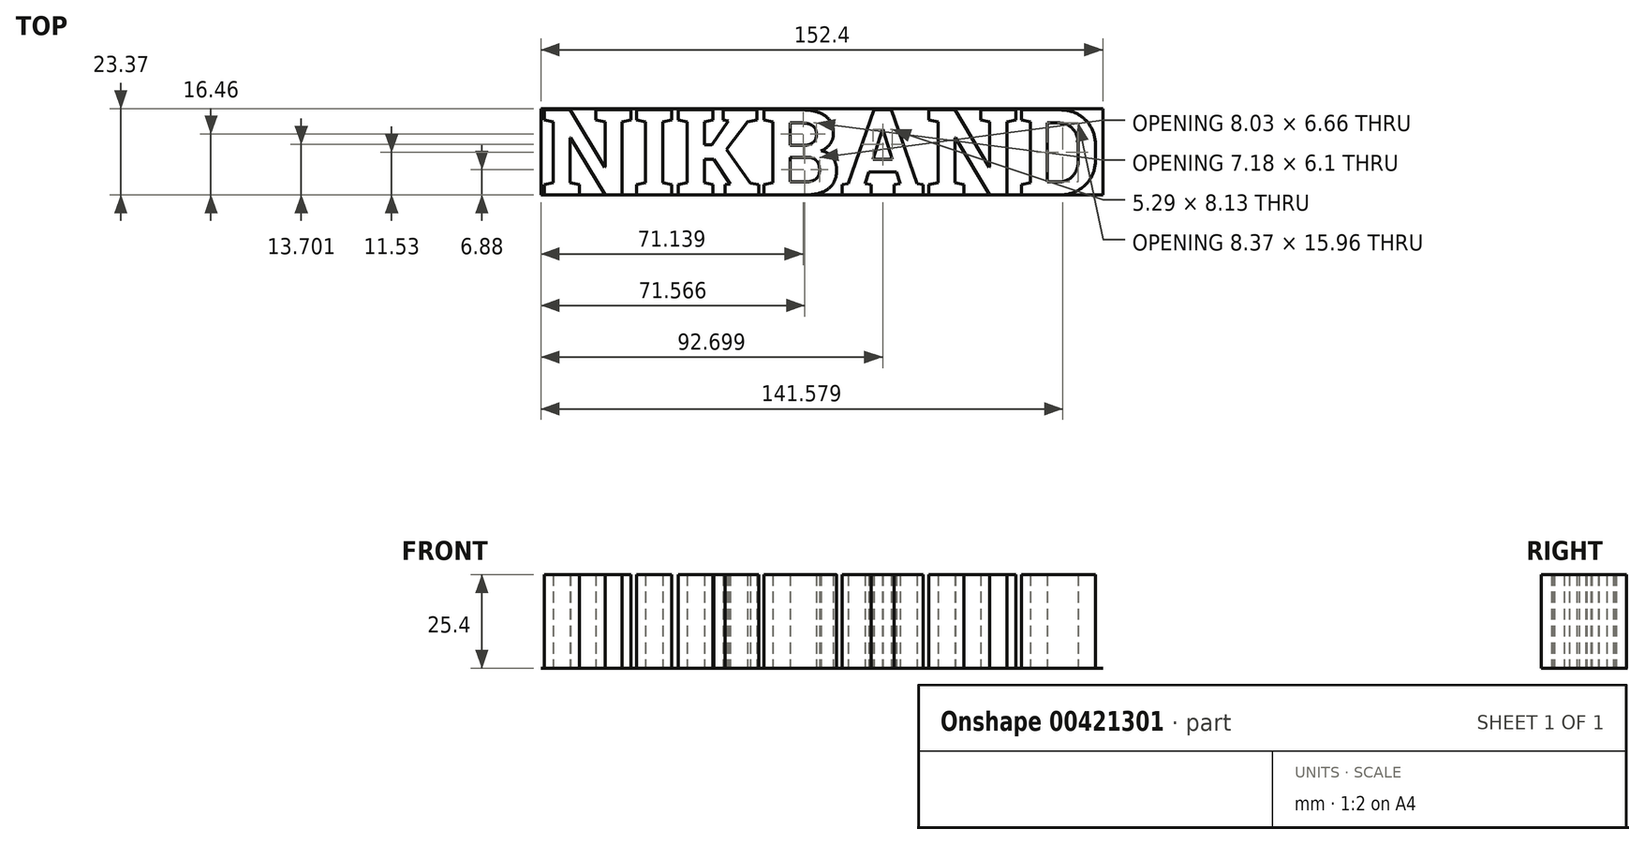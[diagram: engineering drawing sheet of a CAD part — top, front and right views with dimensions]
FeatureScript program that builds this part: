
annotation { "Feature Type Name" : "Feature", "Feature Type Description" : "" }
export const myFeature = defineFeature(function(context is Context, id is Id, definition is map)
    precondition{}
    {
        {
            var Q0;
            Q0=qCreatedBy(makeId("Top.planeOp"),FACE);
            var sketch = newSketch(context, id + "F0", { "sketchPlane" : qUnion([Q0])});
            skText(sketch, "E0", { "text": "NIKBAND ", "fontName": "RobotoSlab-Bold.ttf"});
            skLineSegment(sketch, "E1.bottom", {"start": v(-76.2, -6.03) * mm, "end": v(76.2, -6.03) * mm});
            skLineSegment(sketch, "E1.top", {"start": v(-76.2, 17.34) * mm, "end": v(76.2, 17.34) * mm});
            skLineSegment(sketch, "E1.left", {"start": v(-76.2, -6.03) * mm, "end": v(-76.2, 17.34) * mm});
            skLineSegment(sketch, "E1.right", {"start": v(76.2, -6.03) * mm, "end": v(76.2, 17.34) * mm});
            const initialGuessF0  = {"E0": [-0.0762, -0.00603, 1, 0, 0.02337]};
            skSetInitialGuess(sketch, initialGuessF0);
            skSolve(sketch);
        }
        {
            var Q0;
            Q0 = qSketchRegion(id + "F0", true);
            extrude(context, id + "F1", {"entities" : qUnion([Q0]), "depth" : 1 / 101.6 * mm});
        }
        {
            var Q0;
            Q0=makeQuery(id+"F0.imprint","IMPRINT",FACE,{"disambiguationData":[TD([[makeQuery(id+"F0.imprint","IMPRINT",EDGE,{"derivedFrom":sQuery(id+"F0.wireOp",EDGE,"E0.sketch_text.stroke-0")}),-1.0]])]});
            var Q1;
            Q1=makeQuery(id+"F0.imprint","IMPRINT",FACE,{"disambiguationData":[TD([[makeQuery(id+"F0.imprint","IMPRINT",EDGE,{"derivedFrom":sQuery(id+"F0.wireOp",EDGE,"E0.sketch_text.stroke-24")}),-1.0]])]});
            var Q2;
            Q2=makeQuery(id+"F0.imprint","IMPRINT",FACE,{"disambiguationData":[TD([[makeQuery(id+"F0.imprint","IMPRINT",EDGE,{"derivedFrom":sQuery(id+"F0.wireOp",EDGE,"E0.sketch_text.stroke-36")}),-1.0]])]});
            var Q3;
            Q3=makeQuery(id+"F0.imprint","IMPRINT",FACE,{"disambiguationData":[TD([[makeQuery(id+"F0.imprint","IMPRINT",EDGE,{"derivedFrom":sQuery(id+"F0.wireOp",EDGE,"E0.sketch_text.stroke-65")}),-1.0]])]});
            var Q4;
            Q4=makeQuery(id+"F0.imprint","IMPRINT",FACE,{"disambiguationData":[TD([[makeQuery(id+"F0.imprint","IMPRINT",EDGE,{"derivedFrom":sQuery(id+"F0.wireOp",EDGE,"E0.sketch_text.stroke-95")}),-1.0]])]});
            var Q5;
            Q5=makeQuery(id+"F0.imprint","IMPRINT",FACE,{"disambiguationData":[TD([[makeQuery(id+"F0.imprint","IMPRINT",EDGE,{"derivedFrom":sQuery(id+"F0.wireOp",EDGE,"E0.sketch_text.stroke-115")}),-1.0]])]});
            var Q6;
            Q6=makeQuery(id+"F0.imprint","IMPRINT",FACE,{"disambiguationData":[TD([[makeQuery(id+"F0.imprint","IMPRINT",EDGE,{"derivedFrom":sQuery(id+"F0.wireOp",EDGE,"E0.sketch_text.stroke-139")}),-1.0]])]});
            extrude(context, id + "F2", {"entities" : qUnion([Q0, Q1, Q2, Q3, Q4, Q5, Q6]), "operationType" : NewBodyOperationType.ADD, "depth" : 25.4 * mm});
        }
    });
